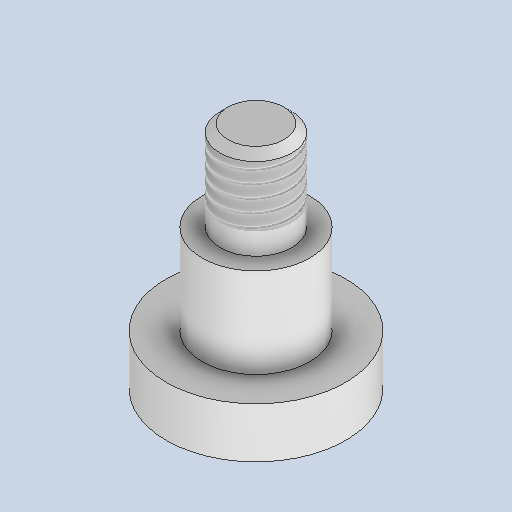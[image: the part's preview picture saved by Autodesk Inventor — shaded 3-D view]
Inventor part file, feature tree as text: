
AUTODESK INVENTOR PART (.ipt)
format: ipt  version: 2024.2 (Build 282272000, 272)  size: 155,136 bytes
history: native  units: mm
features: sketch x2, revolve x1, thread x1, extrude x1, chamfer x1
ambient origin geometry x8: Origin, YZ Plane, XZ Plane, XY Plane, X Axis, Y Axis, Z Axis, Center Point
bodies: Solid1 (feature_tree)
feature tree (6):
  revolve  "Revolution1"  [1 undecoded]
  thread  "Thread1"  [1 undecoded]
  extrude  "Extrusion1"  Depth=5.0mm
  chamfer  "Chamfer1"  Distance=2.8mm
  sketch  "Sketch1"  dims[d0=10.0mm d1=6.0mm d2=4.0mm]
  sketch  "Sketch2"  dims[d3=5.0mm d4=5.0mm d5=2.8mm d6=90.0deg d7=6.0mm d8=1.2mm d9=2.5mm d10=2.0mm d11=0.0mm d12=0.43mm d13=2.0mm d14=45.0deg]
note: 2 required parameter values undecoded (feature->parameter linkage not recoverable at this tier; creation-order binding heuristic only, values carry confidence <= 0.55)